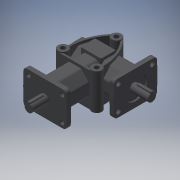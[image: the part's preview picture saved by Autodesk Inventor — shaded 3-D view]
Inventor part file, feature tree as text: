
AUTODESK INVENTOR PART (.ipt)
format: ipt  version: 2018 (Build 220112000, 112)  size: 436,224 bytes
history: native  units: mm
features: sketch x20, extrude x17, hole x2, revolve x1
ambient origin geometry x8: Origin, YZ Plane, XZ Plane, XY Plane, X Axis, Y Axis, Z Axis, Center Point
bodies: Solid1 (feature_tree)
feature tree (40):
  extrude  "Extrusion1"  TaperAngle=360.0deg  [1 undecoded]
  hole  "Hole1"  [1 undecoded]
  revolve  "Revolution1"  [1 undecoded]
  extrude  "Extrusion2"  Depth=31.0mm TaperAngle=0.0deg
  extrude  "Extrusion3"  Depth=66.0mm TaperAngle=0.0deg
  extrude  "Extrusion4"  Depth=66.0mm TaperAngle=0.0deg
  extrude  "Extrusion5"  Depth=66.0mm TaperAngle=0.0deg
  extrude  "Extrusion6"  Depth=8.0mm TaperAngle=0.0deg
  extrude  "Extrusion7"  Depth=60.0mm TaperAngle=0.0deg
  extrude  "Extrusion8"  [1 undecoded]
  extrude  "Extrusion9"  [1 undecoded]
  extrude  "Extrusion10"  [1 undecoded]
  extrude  "Extrusion11"  [1 undecoded]
  extrude  "Extrusion12"  [1 undecoded]
  extrude  "Extrusion13"  [1 undecoded]
  extrude  "Extrusion14"  [1 undecoded]
  extrude  "Extrusion15"  [1 undecoded]
  hole  "Hole2"  [1 undecoded]
  extrude  "Extrusion16"  [1 undecoded]
  extrude  "Extrusion17"  [1 undecoded]
  sketch  "Sketch_1"  dims[d0=8.0mm d1=0.0mm]
  sketch  "Sketch2"  dims[d2=42.0mm d3=6.0mm d4=4.0mm d5=2.0mm d6=90.0deg d7=3.0mm d8=0.0mm d9=360.0deg]
  sketch  "Sketch_3"  dims[d10=9.5mm d11=0.0mm d12=100.0mm d13=0.0mm]
  sketch  "Sketch_5"  dims[d14=132.0mm d15=0.0mm d16=80.0mm d17=0.0mm]
  sketch  "Sketch_6"  dims[d18=41.0mm d19=0.0mm d20=31.0mm d21=0.0mm]
  sketch  "Sketch_7"  dims[d22=62.0mm d23=0.0mm d24=66.0mm d25=0.0mm]
  sketch  "Sketch_9"  dims[d26=66.0mm d27=0.0mm d28=66.0mm d29=0.0mm]
  sketch  "Sketch_10"  dims[d30=66.0mm d31=0.0mm d32=66.0mm d33=0.0mm]
  sketch  "Sketch_11"  dims[d34=66.0mm d35=0.0mm d36=8.0mm d37=0.0mm]
  sketch  "Sketch_12"  dims[d38=42.0mm d39=6.0mm d40=4.0mm d41=2.0mm d42=90.0deg d43=3.0mm d44=0.0mm d45=60.0mm d46=0.0mm]
  sketch  "Sketch_21"
  sketch  "Sketch_13"  dims[d47=9.5mm d48=0.0mm]
  sketch  "Sketch_22"
  sketch  "Sketch_14"
  sketch  "Sketch_23"
  sketch  "Sketch_15"
  sketch  "Sketch_16"
  sketch  "Sketch18"
  sketch  "Sketch_18"
  sketch  "Sketch_20"
note: 14 required parameter values undecoded (feature->parameter linkage not recoverable at this tier; creation-order binding heuristic only, values carry confidence <= 0.55)